# Revit family: ASSA_ABLOY_DockLeveler_DL6210S
name_source: partatom
category: Specialty Equipment
units: mm (PartAtom-declared; Revit-internal decimal feet)

## family parameters
Always vertical = Yes
Cut with Voids When Loaded = No
Host = Floor
Part Type = Normal
Room Calculation Point = No
Round Connector Dimension = Use Diameter
Shared = No

## types (2) — shared parameters
BentLip = No
CrossFrontBeamHeight = 480 mm  [stored 1.5748 ft]
DL6210SBentLip = DL6210S_Platform : DL6210S_BentLip
DL6210SStraightLip = DL6210S_Platform : DL6210S_StraightLip
Description = Dock Leveler
FloorThickness = 1250 mm  [stored 4.10105 ft]
FrameT200 = No
Manufacturer = ASSA ABLOY
Model = DL6210S
StraightLip = Yes
TailLiftWidth = 3000 mm  [stored 9.84252 ft]

## per-type parameters (varying)
| type | LipType |
| DL6210S_BentLip | DL6210S_Platform : DL6210S_BentLip |
| DL6210S_StraightLip | DL6210S_Platform : DL6210S_StraightLip |

note: [stored X ft] marks values corroborated as IEEE doubles in the binary element streams (Revit-internal decimal feet)

## geometry (parser evidence)
native form markers: Sweep x18
no freeform markers — native parametric forms only
